# Revit family: Domotics-DomesticRanges-GEWISS-CHORUS_COMMAND-PUSH-BUTTON_KEY
name_source: partatom
category: Apparecchi elettrici
revit_build: Autodesk Revit 2016 (Build: 20161004_0715(x64)
units: mm (PartAtom-declared; Revit-internal decimal feet)

## family parameters
Condiviso = Sì
Host = Superficie
Mantenere orientamento annotazione = Sì
Numero OmniClass = 23.80.50.11.14
Punto di calcolo locali = Sì
Quota connettore circolare = Usa diametro
Taglio con vuoti quando caricato = Sì
Tipo di parte = Normale
Titolo OmniClass = Switches

## types (3) — shared parameters
Breaking capacity: = 1.25 In (200 position changes)
Button key = With key
Catalogue = DOMOTICS
Catalogue Range = CHORUS - DOMESTIC RANGE
Category = Push-button
Description: = 2P NO - 10A
Electrocod = 0130
Glow Wire Test = 850°C
IDF = 5fd6d463-05ee-4339-a18f-7d27da771289
IDT = 35582b85-b638-43e4-b97c-50c41eb5cacb
Immagine tipo = GW14145.jpg
Insulation resistance = > 5 MOhm
Larghezza pulsante = 23 mm  [stored 0.0754593 ft]
No. Chorus modules = 1
Number of poles = 2P
Produttore = GEWISS S.p.A.
Prolonged operation (no.of position changes) = 40.000 at In 250 V ac cosÃ˜=0,6
Prospetto di default = 1219 mm
Resistance at test voltage = 2000 V at 50 Hz for 1 minute
SEO = Push button
Simbolo_ = SIMBOLO PULSANTI : PULSCHIAVE
Standard; = EN 60669-1
Technical sheet = https://www.gewiss.com
Terminal grip on cable traction = > 50 N
Terminal tightening capacity flexible cables (mm2) = min. 0,75 - max. 2x4
Terminal tightening capacity rigid cables (mm2) = min. 0,5 - max. 2x2,5
Thermo-pressure with ball = 125
Tipo_ = CHORUS PULSANTI CHIAVE_BASE : GW14145 - Titanio
Type = With key
URL = https://www.gewiss.com
Version file RFA = 19.0
Voltage = 250 V ac
Voltage: = 250 V ac
Wiring terminals = With screw

## per-type parameters (varying)
| type | Colour | Descrizione | EAN code | Modello |
| GW12145 - Black | Black | PUSH-BUTTON 1M 2P NO 10A+KEY, BLACK | 8011564268067 | GW12145 |
| GW14145 - Titanium | Titanium | PUSH-BUTTON 1M 2P NO 10A+KEY TITANIUM | 8011564265974 | GW14145 |
| GW10145 - White | White | PUSH-BUTTON, 1M 2P NO 10A+KEY, WHITE | 8011564261877 | GW10145 |

note: source unit labels omitted for Thermo-pressure with ball — the stored unit's dimension contradicts the parameter name (converter mislabeling)

note: [stored X ft] marks values corroborated as IEEE doubles in the binary element streams (Revit-internal decimal feet)

## geometry (parser evidence)
native form markers: Sweep x2
no freeform markers — native parametric forms only
